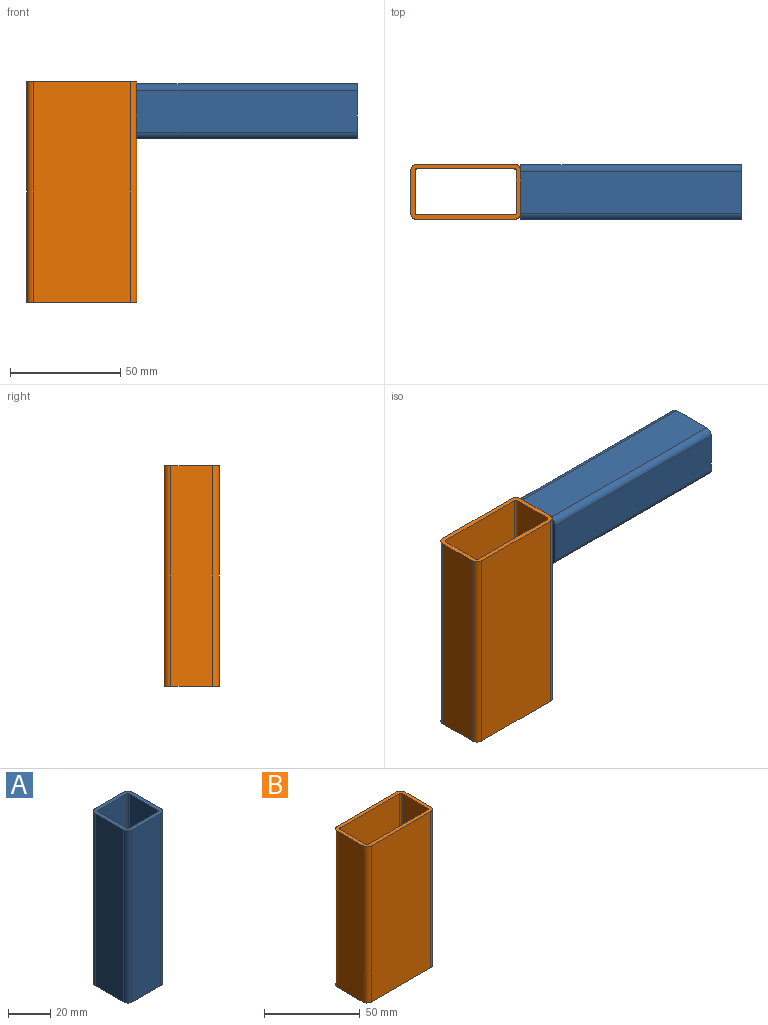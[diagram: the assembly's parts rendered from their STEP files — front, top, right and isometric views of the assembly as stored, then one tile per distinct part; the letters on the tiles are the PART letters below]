
ASSEMBLY  parts=2 mates=1
PART A: 18 faces, bbox 25x25x100 mm
  f0: plane 100x19mm, normal (1,0,0), area 1900mm2, adj f1,f15,f16,f17
  f1: cylinder r=3mm len=100mm, axis (0,0,-1), area 471.2mm2, adj f0,f2,f16,f17
  f2: plane 100x19mm, normal (0,1,0), area 1900mm2, adj f1,f3,f16,f17
  f3: cylinder r=3mm len=100mm, axis (0,0,-1), area 471.2mm2, adj f2,f4,f16,f17
  f4: plane 100x19mm, normal (-1,0,0), area 1900mm2, adj f3,f5,f16,f17
  f5: cylinder r=3mm len=100mm, axis (0,0,-1), area 471.2mm2, adj f4,f6,f16,f17
  f6: plane 100x19mm, normal (0,-1,0), area 1900mm2, adj f5,f15,f16,f17
  f7: cylinder r=1mm len=100mm, axis (0,0,-1), area 157.1mm2, adj f8,f14,f16,f17
  f8: plane 100x19mm, normal (1,0,0), area 1900mm2, adj f7,f9,f16,f17
  f9: cylinder r=1mm len=100mm, axis (0,0,-1), area 157.1mm2, adj f8,f10,f16,f17
  f10: plane 100x19mm, normal (0,-1,0), area 1900mm2, adj f9,f11,f16,f17
  f11: cylinder r=1mm len=100mm, axis (0,0,-1), area 157.1mm2, adj f10,f12,f16,f17
  f12: plane 100x19mm, normal (-1,0,0), area 1900mm2, adj f11,f13,f16,f17
  f13: cylinder r=1mm len=100mm, axis (0,0,-1), area 157.1mm2, adj f12,f14,f16,f17
  f14: plane 100x19mm, normal (0,1,0), area 1900mm2, adj f7,f13,f16,f17
  f15: cylinder r=3mm len=100mm, axis (0,0,-1), area 471.2mm2, adj f0,f6,f16,f17
  f16: plane 25x25mm, normal (0,0,1), area 177.1mm2, adj f0,f1,f2,f3,f4,f5,f6,f7
  f17: plane 25x25mm, normal (0,0,-1), area 177.1mm2, adj f0,f1,f2,f3,f4,f5,f6,f7
PART B: 18 faces, bbox 50x25x100 mm
  f0: plane 100x44mm, normal (0,-1,0), area 4400mm2, adj f1,f15,f16,f17
  f1: cylinder r=3mm len=100mm, axis (0,0,-1), area 471.2mm2, adj f0,f2,f16,f17
  f2: plane 100x19mm, normal (1,0,0), area 1900mm2, adj f1,f3,f16,f17
  f3: cylinder r=3mm len=100mm, axis (0,0,-1), area 471.2mm2, adj f2,f4,f16,f17
  f4: plane 100x44mm, normal (0,1,0), area 4400mm2, adj f3,f5,f16,f17
  f5: cylinder r=3mm len=100mm, axis (0,0,-1), area 471.2mm2, adj f4,f6,f16,f17
  f6: plane 100x19mm, normal (-1,0,0), area 1900mm2, adj f5,f15,f16,f17
  f7: cylinder r=1mm len=100mm, axis (0,0,-1), area 157.1mm2, adj f8,f14,f16,f17
  f8: plane 100x19mm, normal (1,0,0), area 1900mm2, adj f7,f9,f16,f17
  f9: cylinder r=1mm len=100mm, axis (0,0,-1), area 157.1mm2, adj f8,f10,f16,f17
  f10: plane 100x44mm, normal (0,-1,0), area 4400mm2, adj f9,f11,f16,f17
  f11: cylinder r=1mm len=100mm, axis (0,0,-1), area 157.1mm2, adj f10,f12,f16,f17
  f12: plane 100x19mm, normal (-1,0,0), area 1900mm2, adj f11,f13,f16,f17
  f13: cylinder r=1mm len=100mm, axis (0,0,-1), area 157.1mm2, adj f12,f14,f16,f17
  f14: plane 100x44mm, normal (0,1,0), area 4400mm2, adj f7,f13,f16,f17
  f15: cylinder r=3mm len=100mm, axis (0,0,-1), area 471.2mm2, adj f0,f6,f16,f17
  f16: plane 50x25mm, normal (0,0,1), area 277.1mm2, adj f0,f1,f2,f3,f4,f5,f6,f7
  f17: plane 50x25mm, normal (0,0,-1), area 277.1mm2, adj f0,f1,f2,f3,f4,f5,f6,f7
PLACE A rot(axis=(0.71,0,-0.71),180deg) t=(125.03,-0.2,86.55)mm
PLACE B at identity
MATE parallel A.f16 <-> B.f2  axis (-1,0,0) through (25.03,-0.2,86.55)mm
